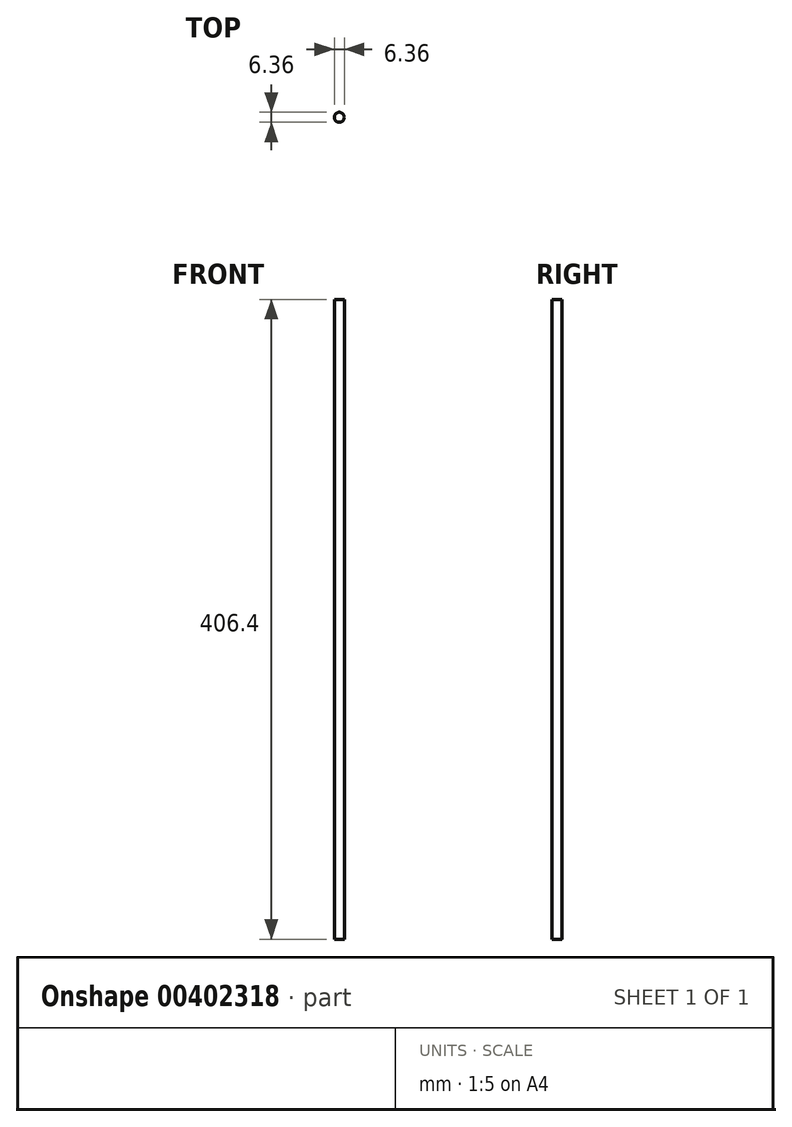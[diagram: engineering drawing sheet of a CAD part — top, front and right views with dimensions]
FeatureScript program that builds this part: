
annotation { "Feature Type Name" : "Feature", "Feature Type Description" : "" }
export const myFeature = defineFeature(function(context is Context, id is Id, definition is map)
    precondition{}
    {
        {
            var Q0;
            Q0=qCreatedBy(makeId("Top.planeOp"),FACE);
            var sketch = newSketch(context, id + "F0", { "sketchPlane" : qUnion([Q0])});
            skCircle(sketch, "E0", {"center": v(0, 0) * mm, "radius": 3.17 * mm});
            skSolve(sketch);
        }
        {
            var Q0;
            Q0 = qSketchRegion(id + "F0", true);
            extrude(context, id + "F1", {"entities" : qUnion([Q0]), "depth" : 406.4 * mm, "symmetric" : true});
        }
    });
